# Revit family: K12.2 - Freespace
name_source: partatom
category: Communication Devices
revit_build: Autodesk Revit 2017 (Build: 20190508_0315(x64)
units: mm (PartAtom-declared; Revit-internal decimal feet)

## family parameters
Always vertical = No
Cut with Voids When Loaded = No
Maintain Annotation Orientation = No
Part Type = Normal
Room Calculation Point = No
Round Connector Dimension = Use Diameter
Shared = No
Work Plane-Based = Yes

## types (1)
- K12.2 - Freespace
    Coverage Horizontal = 75.00°
    Coverage Vertical = 75.00°
    Default Elevation = 0' - 0"
    Depth = 1' - 1 13/16"
    Description = Multi-purpose, 2-way active loudspeaker
    Height = 1' - 11 11/16"
    Manufacturer = QSC
    Manufacturer URL = qsc.com
    Model = K12.2
    Product Documentation Link = https://www.qsc.com
    Product Page URL = https://www.qsc.com
    Regulatory Compliance = CE, RAEE, UL, China RoHS, RoHS II, FCC Class B
    SPL Max = 132
    Weight Dimensional (kg) = 21.7
    Weight Dimensional (lb) = 47.8
    Weight Product (kg) = 17.7
    Weight Product (lb) = 39
    Width = 1' - 2"

## geometry (parser evidence)
native form markers: Blend x4, Sweep x7
no freeform markers — native parametric forms only
